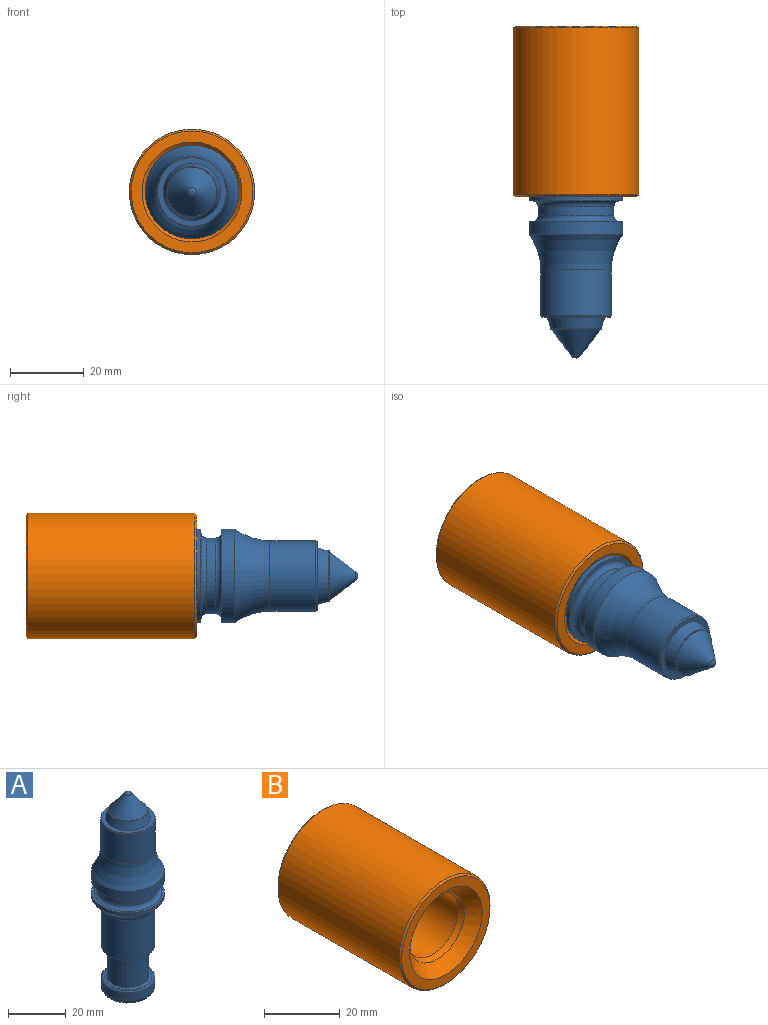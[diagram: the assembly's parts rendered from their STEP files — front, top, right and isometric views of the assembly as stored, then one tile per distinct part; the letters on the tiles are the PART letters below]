
ASSEMBLY  parts=2 mates=1
PART A: 28 faces, bbox 30.7x30.7x84.4 mm
  f0: cone r=7.8mm half-angle=17.5deg, axis (0,0,-1), area 152mm2, adj f1,f27
  f1: cylinder r=6.81mm len=13.61mm, axis (0,0,-1), area 7.1mm2, adj f0,f2
  f2: plane 13.61x13.61mm, normal (0,0,1), area 5.4mm2, adj f1,f3
  f3: cone r=6.68mm half-angle=37.5deg, axis (0,0,-1), area 222.6mm2, adj f2,f4
  f4: sphere r=1.52mm, area 5.7mm2, adj f3
  f5: plane 14.35x14.35mm, normal (0,0,-1), area 161.8mm2, adj f6
  f6: torus R=7.18mm, axis (0,0,-1), area 182.2mm2, adj f5,f7
  f7: cylinder r=9.33mm len=18.67mm, axis (0,0,-1), area 186.2mm2, adj f6,f8
  f8: torus R=8.83mm, axis (0,0,-1), area 45.9mm2, adj f7,f9
  f9: plane 17.65x17.65mm, normal (0,0,1), area 33.9mm2, adj f8,f10
  f10: torus R=8.19mm, axis (0,0,-1), area 48.4mm2, adj f9,f11
  f11: cone r=7.26mm half-angle=0deg, axis (0,0,-1), area 579.5mm2, adj f10,f12
  f12: torus R=8.19mm, axis (0,0,-1), area 48.5mm2, adj f11,f13
  f13: plane 18.67x18.67mm, normal (0,0,-1), area 62.9mm2, adj f12,f14
  f14: cylinder r=9.33mm len=18.67mm, axis (0,0,-1), area 987.3mm2, adj f13,f15
  f15: torus R=11.62mm, axis (0,0,-1), area 107.9mm2, adj f14,f16
  f16: cone r=10mm half-angle=45deg, axis (0,0,1), area 271.9mm2, adj f15,f17
  f17: cylinder r=12.7mm len=25.4mm, axis (0,0,-1), area 114.5mm2, adj f16,f18
  f18: plane 25.4x25.4mm, normal (0,0,1), area 68.5mm2, adj f17,f19
  f19: torus R=11.81mm, axis (0,0,-1), area 163.1mm2, adj f18,f20
  f20: cylinder r=10.29mm len=20.57mm, axis (0,0,-1), area 164.2mm2, adj f19,f21
  f21: torus R=11.81mm, axis (0,0,-1), area 163.1mm2, adj f20,f22
  f22: plane 25.4x25.4mm, normal (0,0,-1), area 68.5mm2, adj f21,f23
  f23: cylinder r=12.7mm len=25.4mm, axis (0,0,-1), area 283.8mm2, adj f22,f24
  f24: torus R=25.53mm, axis (0,0,-1), area 682.9mm2, adj f23,f25
  f25: cylinder r=9.52mm len=19.05mm, axis (0,0,-1), area 745.4mm2, adj f24,f26
  f26: cone r=9.52mm half-angle=30deg, axis (0,0,-1), area 26mm2, adj f25,f27
  f27: plane 18.61x18.61mm, normal (0,0,1), area 80.8mm2, adj f0,f26
PART B: 15 faces, bbox 34x46.3x34 mm
  f0: cylinder r=9.55mm len=19.1mm, axis (0,-1,0), area 609mm2, adj f8,f12
  f1: cylinder r=9.55mm len=19.1mm, axis (0,-1,0), area 939.1mm2, adj f9,f11
  f2: cylinder r=17mm len=45.3mm, axis (0,-1,0), area 4838.7mm2, adj f13,f14
  f3: plane 33x33mm, normal (0,1,0), area 538mm2, adj f12,f13
  f4: plane 33x33mm, normal (0,-1,0), area 278.5mm2, adj f10,f14
  f5: plane 21x21mm, normal (0,-1,0), area 29.1mm2, adj f7,f8
  f6: plane 21x21mm, normal (0,1,0), area 29.1mm2, adj f7,f9
  f7: cylinder r=10.5mm len=21mm, axis (0,-1,0), area 923.6mm2, adj f5,f6
  f8: cone r=10.05mm half-angle=45deg, axis (0,-1,0), area 43.5mm2, adj f0,f5
  f9: cone r=9.55mm half-angle=45deg, axis (0,1,0), area 43.5mm2, adj f1,f6
  f10: cone r=9.55mm half-angle=45deg, axis (0,-1,0), area 348.3mm2, adj f4,f11
  f11: cone r=9.55mm half-angle=22.5deg, axis (0,-1,0), area 115mm2, adj f1,f10
  f12: cone r=10.05mm half-angle=45deg, axis (0,1,0), area 43.5mm2, adj f0,f3
  f13: cone r=17mm half-angle=45deg, axis (0,-1,0), area 74.4mm2, adj f2,f3
  f14: cone r=16.5mm half-angle=45deg, axis (0,1,0), area 74.4mm2, adj f2,f4
PLACE A rot(axis=(1,0,0),90deg) t=(106.8,-72.35,4.05)mm
PLACE B t=(-6.89,-24.43,4.05)mm fixed
MATE revolute A.f0 <-> B.f7  axis (0,1,0) through (-6.89,3.72,4.05)mm
